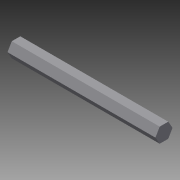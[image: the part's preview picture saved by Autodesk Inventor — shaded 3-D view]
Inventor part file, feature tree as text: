
AUTODESK INVENTOR PART (.ipt)
format: ipt  version: 2015 SP1 (Build 190203100, 203)  size: 77,312 bytes
history: native  units: in
note: dims shown in document units (in); Inventor stores cm internally (conversion verified against a paired STEP export)
features: extrude x1, sketch x1
ambient origin geometry x8: Origin, YZ Plane, XZ Plane, XY Plane, X Axis, Y Axis, Z Axis, Center Point
bodies: Solid1 (feature_tree)
feature tree (2):
  extrude  "Extrusion1"  TaperAngle=30.0deg  [1 undecoded]
  sketch  "Sketch1"  dims[d0=0.5in d1=30.0deg d2=30.0deg d3=2.3622in d5=360.0deg d7=6.0in d8=0.0in]
note: 1 required parameter value undecoded (feature->parameter linkage not recoverable at this tier; creation-order binding heuristic only, values carry confidence <= 0.55)
